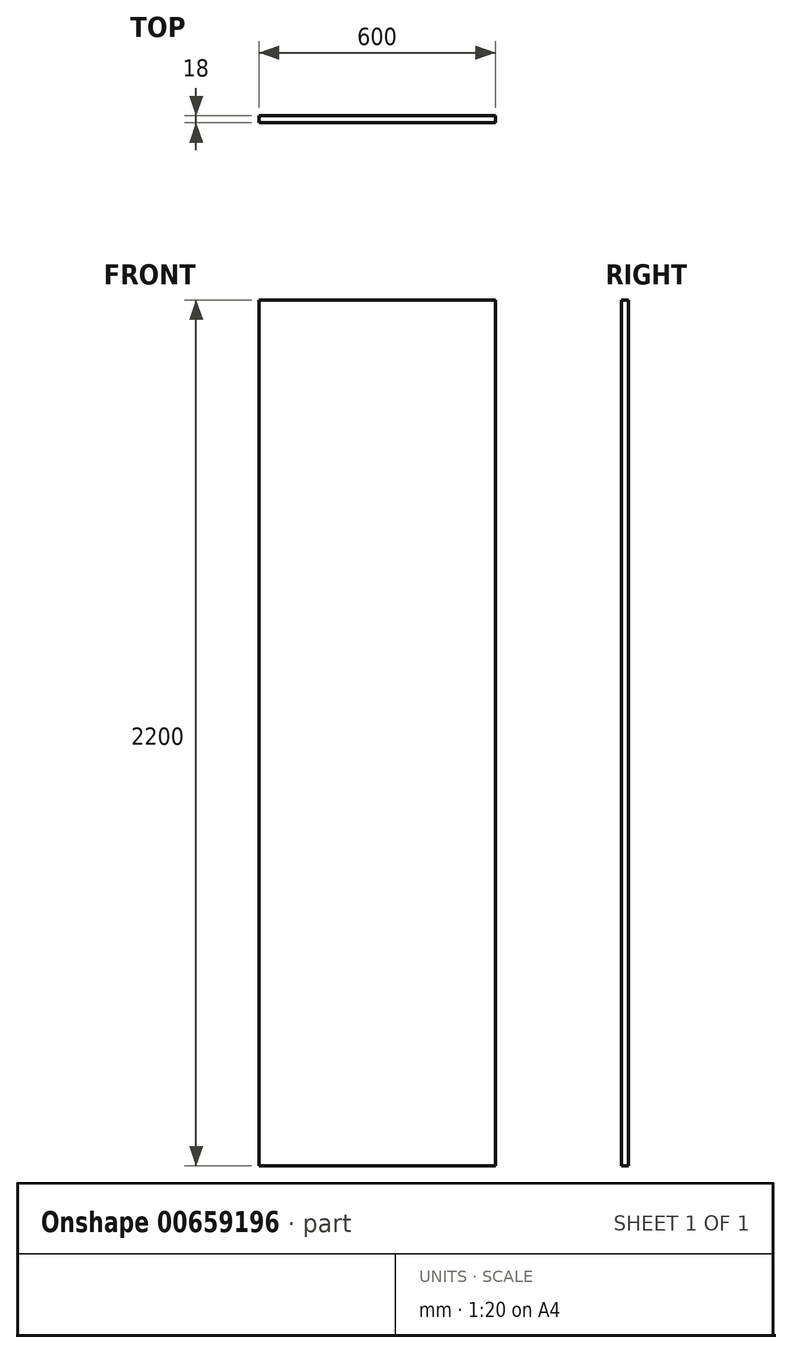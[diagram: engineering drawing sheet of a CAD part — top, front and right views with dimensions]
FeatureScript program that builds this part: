
annotation { "Feature Type Name" : "Feature", "Feature Type Description" : "" }
export const myFeature = defineFeature(function(context is Context, id is Id, definition is map)
    precondition{}
    {
        {
            var Q0;
            Q0=qCreatedBy(makeId("Front.planeOp"),FACE);
            var sketch = newSketch(context, id + "F0", { "sketchPlane" : qUnion([Q0])});
            skLineSegment(sketch, "E0.bottom", {"start": v(-308.27, 1994.83) * mm, "end": v(291.73, 1994.83) * mm});
            skLineSegment(sketch, "E0.top", {"start": v(-308.27, -205.17) * mm, "end": v(291.73, -205.17) * mm});
            skLineSegment(sketch, "E0.left", {"start": v(-308.27, 1994.83) * mm, "end": v(-308.27, -205.17) * mm});
            skLineSegment(sketch, "E0.right", {"start": v(291.73, 1994.83) * mm, "end": v(291.73, -205.17) * mm});
            skSolve(sketch);
        }
        {
            var Q0;
            Q0=makeQuery(id+"F0.imprint","IMPRINT",FACE,{"disambiguationData":[TD([[makeQuery(id+"F0.imprint","IMPRINT",EDGE,{"derivedFrom":sQuery(id+"F0.wireOp",EDGE,"E0.bottom")}),-1.0]])]});
            extrude(context, id + "F1", {"entities" : qUnion([Q0]), "endBound" : BoundingType.SYMMETRIC, "depth" : 18 * mm, "offsetDistance" : 25 * mm});
        }
    });
